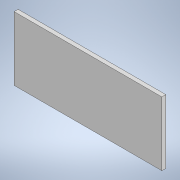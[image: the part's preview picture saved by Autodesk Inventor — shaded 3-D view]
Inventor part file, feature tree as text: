
AUTODESK INVENTOR PART (.ipt)
format: ipt  version: 2020.2 (Build 242310000, 310)  size: 95,232 bytes
history: native  units: mm
features: extrude x1, sketch x1
ambient origin geometry x8: Origin, YZ Plane, XZ Plane, XY Plane, X Axis, Y Axis, Z Axis, Center Point
bodies: Solide1 (feature_tree)
feature tree (2):
  extrude  "Extrusion1"  Depth=148.0mm
  sketch  "Esquisse1"
